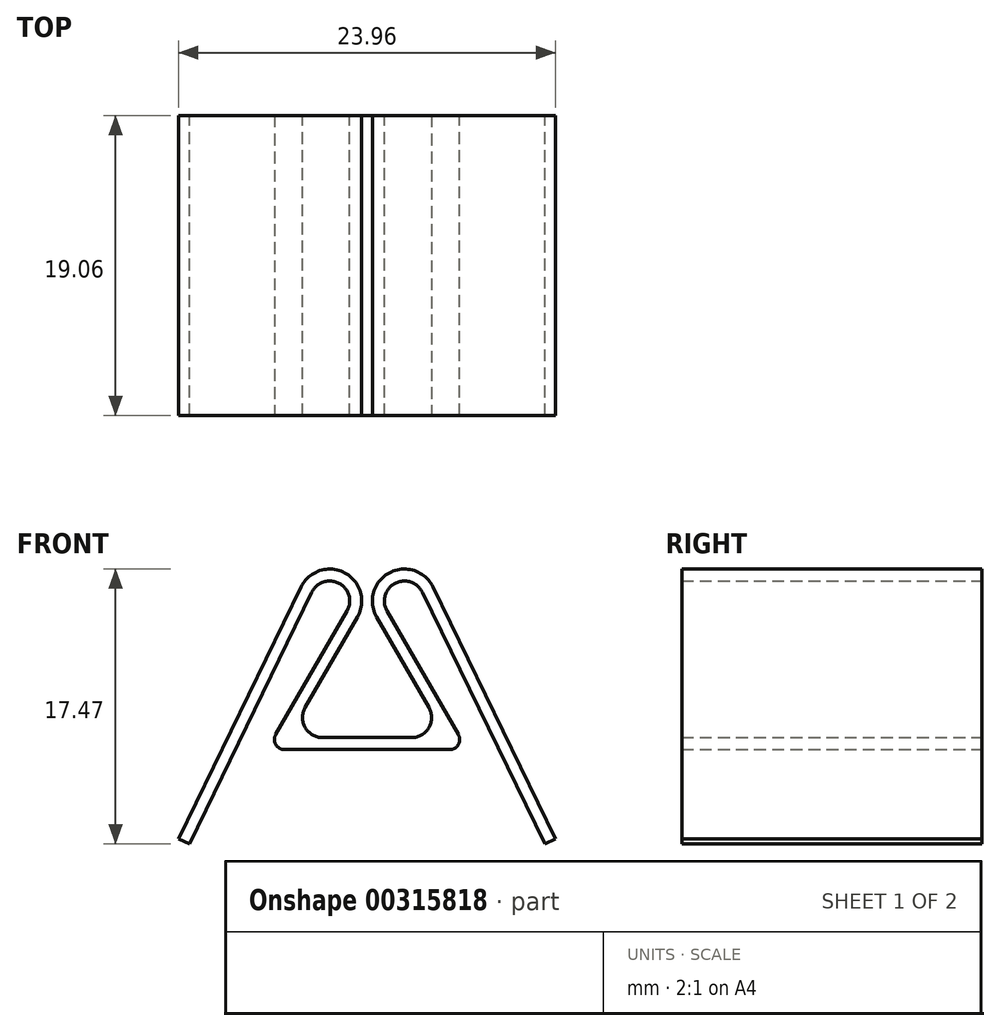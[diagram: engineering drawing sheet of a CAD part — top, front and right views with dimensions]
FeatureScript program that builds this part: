
annotation { "Feature Type Name" : "Feature", "Feature Type Description" : "" }
export const myFeature = defineFeature(function(context is Context, id is Id, definition is map)
    precondition{}
    {
        {
            var Q0;
            Q0=qCreatedBy(makeId("Front.planeOp"),FACE);
            var sketch = newSketch(context, id + "F0", { "sketchPlane" : qUnion([Q0])});
            skLineSegment(sketch, "E0", {"start": v(0, 0) * mm, "end": v(6.35, 0) * mm});
            skLineSegment(sketch, "E1", {"start": v(6.35, 0) * mm, "end": v(1.27, 8.8) * mm});
            skArc(sketch, "E2", {"start": v(3.51, 9.99) * mm, "mid": v(1.77, 10.56) * mm, "end": v(1.27, 8.8) * mm});
            skLineSegment(sketch, "E3.2", {"start": v(0, 0.76) * mm, "end": v(5.03, 0.76) * mm});
            skLineSegment(sketch, "E3.3", {"start": v(5.03, 0.76) * mm, "end": v(0.61, 8.42) * mm});
            skArc(sketch, "E3.4", {"start": v(4.2, 10.32) * mm, "mid": v(1.42, 11.23) * mm, "end": v(0.61, 8.42) * mm});
            skLineSegment(sketch, "E4", {"start": v(4.2, 10.32) * mm, "end": v(11.98, -5.67) * mm});
            skLineSegment(sketch, "E5", {"start": v(11.98, -5.67) * mm, "end": v(11.3, -6) * mm});
            skLineSegment(sketch, "E6", {"start": v(11.3, -6) * mm, "end": v(3.51, 9.99) * mm});
            skLineSegment(sketch, "E7", {"start": v(0, 0) * mm, "end": v(0, 0.76) * mm});
            skLineSegment(sketch, "E8.0.MirrorCS", {"start": v(0, 0.76) * mm, "end": v(-5.03, 0.76) * mm});
            skLineSegment(sketch, "E9.0.MirrorCS", {"start": v(-5.03, 0.76) * mm, "end": v(-0.61, 8.42) * mm});
            skLineSegment(sketch, "E10.0.MirrorCS", {"start": v(-6.35, 0) * mm, "end": v(-1.27, 8.8) * mm});
            skArc(sketch, "E11.0.MirrorCS", {"start": v(-3.51, 9.99) * mm, "mid": v(-1.77, 10.56) * mm, "end": v(-1.27, 8.8) * mm});
            skArc(sketch, "E12.0.MirrorCS", {"start": v(-4.2, 10.32) * mm, "mid": v(-1.42, 11.23) * mm, "end": v(-0.61, 8.42) * mm});
            skLineSegment(sketch, "E13.0.MirrorCS", {"start": v(-11.3, -6) * mm, "end": v(-3.51, 9.99) * mm});
            skLineSegment(sketch, "E14.0.MirrorCS", {"start": v(-4.2, 10.32) * mm, "end": v(-11.98, -5.67) * mm});
            skLineSegment(sketch, "E15.0.MirrorCS", {"start": v(0, 0) * mm, "end": v(-6.35, 0) * mm});
            skLineSegment(sketch, "E16.0.MirrorCS", {"start": v(-11.98, -5.67) * mm, "end": v(-11.3, -6) * mm});
            skSolve(sketch);
        }
        {
            var Q0;
            Q0=qSketchRegion(id+"F0",true);
            extrude(context, id + "F1", {"entities" : qUnion([Q0]), "endBound" : BoundingType.SYMMETRIC, "depth" : 19.05 * mm});
        }
        {
            var Q0;
            Q0=makeQuery(id+"F1.opExtrude","SWEPT_EDGE",EDGE,{"disambiguationData":[OSD([sQuery(id+"F0.wireOp",EDGE,"E0"),sQuery(id+"F0.wireOp",EDGE,"E1")])]});
            var Q1;
            Q1=makeQuery(id+"F1.opExtrude","SWEPT_EDGE",EDGE,{"disambiguationData":[OSD([sQuery(id+"F0.wireOp",EDGE,"E10.0.MirrorCS"),sQuery(id+"F0.wireOp",EDGE,"E15.0.MirrorCS")])]});
            fillet(context, id + "F2", {"entities" : qUnion([Q0, Q1]), "radius" : 0.64 * mm, "tangentPropagation" : true, "allowEdgeOverflow" : false});
        }
        {
            var Q0;
            Q0=makeQuery(id+"F1.opExtrude","SWEPT_EDGE",EDGE,{"disambiguationData":[OSD([sQuery(id+"F0.wireOp",EDGE,"E3.2"),sQuery(id+"F0.wireOp",EDGE,"E3.3")])]});
            var Q1;
            Q1=makeQuery(id+"F1.opExtrude","SWEPT_EDGE",EDGE,{"disambiguationData":[OSD([sQuery(id+"F0.wireOp",EDGE,"E8.0.MirrorCS"),sQuery(id+"F0.wireOp",EDGE,"E9.0.MirrorCS")])]});
            fillet(context, id + "F3", {"entities" : qUnion([Q0, Q1]), "radius" : 1.27 * mm, "tangentPropagation" : true, "allowEdgeOverflow" : false});
        }
    });
